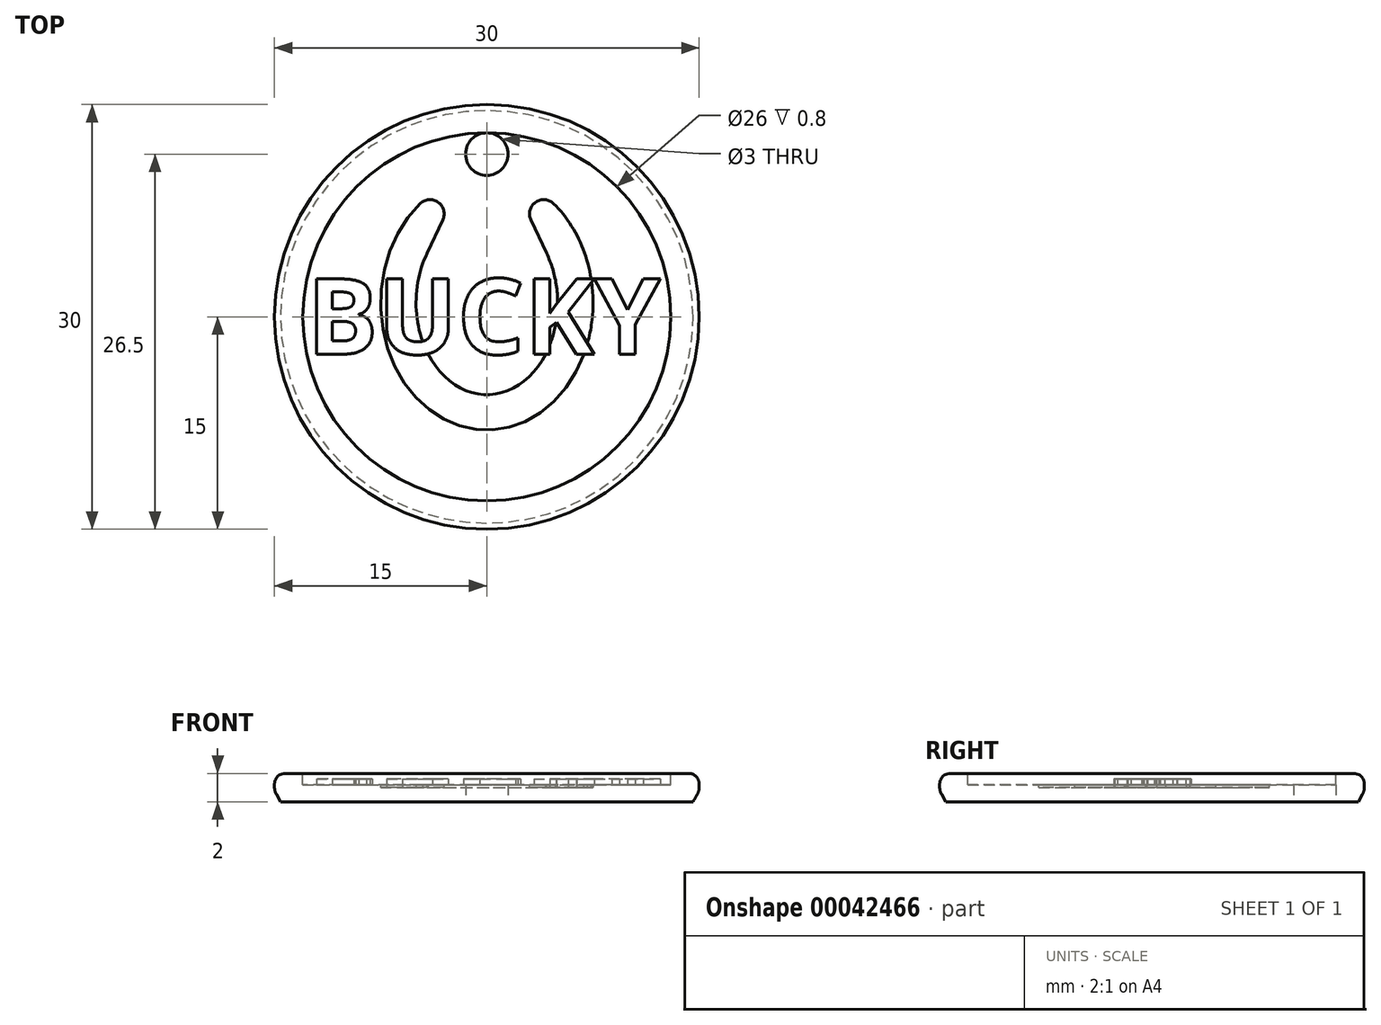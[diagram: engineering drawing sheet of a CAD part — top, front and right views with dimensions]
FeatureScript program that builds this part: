
annotation { "Feature Type Name" : "Feature", "Feature Type Description" : "" }
export const myFeature = defineFeature(function(context is Context, id is Id, definition is map)
    precondition{}
    {
        {
            var Q0;
            Q0=qCreatedBy(makeId("Top.planeOp"),FACE);
            var sketch = newSketch(context, id + "F0", { "sketchPlane" : qUnion([Q0])});
            skCircle(sketch, "E0", {"center": v(0, 0) * mm, "radius": 15 * mm});
            skSolve(sketch);
        }
        {
            var Q0;
            Q0=qSketchRegion(id+"F0",true);
            extrude(context, id + "F1", {"entities" : qUnion([Q0]), "depth" : 2 * mm});
        }
        {
            var Q0;
            Q0=makeQuery(id+"F1.opExtrude","CAP_FACE",FACE,{"disambiguationData":[OSD([sQuery(id+"F0.wireOp",EDGE,"E0")])],"isStart":false});
            var sketch = newSketch(context, id + "F2", { "sketchPlane" : qUnion([Q0])});
            skCircle(sketch, "E1", {"center": v(0, 0) * mm, "radius": 13 * mm});
            skSolve(sketch);
        }
        {
            var Q0;
            Q0=qSketchRegion(id+"F2",true);
            extrude(context, id + "F3", {"entities" : qUnion([Q0]), "operationType" : NewBodyOperationType.REMOVE, "oppositeDirection" : true, "depth" : 0.8 * mm});
        }
        {
            var Q0;
            Q0=makeQuery(id+"F3.boolean.opBoolean","COPY",FACE,{"derivedFrom":makeQuery(id+"F3.opExtrude","CAP_FACE",FACE,{"disambiguationData":[OSD([sQuery(id+"F2.wireOp",EDGE,"E1")])],"isStart":false})});
            var sketch = newSketch(context, id + "F4", { "sketchPlane" : qUnion([Q0])});
            skLineSegment(sketch, "E2", {"start": v(-7.5, -8) * mm, "end": v(7.5, 8) * mm, "construction": true});
            skEllipticalArc(sketch, "E3", {});
            skEllipticalArc(sketch, "E4", {});
            skLineSegment(sketch, "E5", {"start": v(-4.21, 4.5) * mm, "end": v(-3.11, 6.86) * mm});
            skArc(sketch, "E6", {"start": v(-3.11, 6.86) * mm, "mid": v(-3.44, 8.1) * mm, "end": v(-4.72, 8) * mm});
            skArc(sketch, "E7.MirrorCS", {"start": v(3.11, 6.86) * mm, "mid": v(3.44, 8.1) * mm, "end": v(4.72, 8) * mm});
            skLineSegment(sketch, "E8.MirrorCS", {"start": v(4.21, 4.5) * mm, "end": v(3.11, 6.86) * mm});
            const initialGuessF4  = {"E3": [0, 0.001, 0, -1, 0.0065, 0.005, 4.143778680120507, 2.1394066270590786], "E4": [0, 0.001, 0, -1, 0.009, 0.0075, 3.821776784577257, 2.461408522602329]};
            skSetInitialGuess(sketch, initialGuessF4);
            skSolve(sketch);
        }
        {
            var Q0;
            Q0=qSketchRegion(id+"F4",true);
            extrude(context, id + "F5", {"entities" : qUnion([Q0]), "operationType" : NewBodyOperationType.REMOVE, "oppositeDirection" : true, "depth" : 0.2 * mm});
        }
        {
            var Q0;
            Q0=qCreatedBy(makeId("Top.planeOp"),FACE);
            var sketch = newSketch(context, id + "F6", { "sketchPlane" : qUnion([Q0])});
            skLineSegment(sketch, "E9", {"start": v(0, 0.05) * mm, "end": v(0, -0.05) * mm, "construction": true});
            skSolve(sketch);
        }
        {
            var Q0;
            Q0=makeQuery(id+"F3.boolean.opBoolean","COPY",FACE,{"derivedFrom":makeQuery(id+"F3.opExtrude","CAP_FACE",FACE,{"disambiguationData":[OSD([sQuery(id+"F2.wireOp",EDGE,"E1")])],"isStart":false})});
            var sketch = newSketch(context, id + "F7", { "sketchPlane" : qUnion([Q0])});
            skText(sketch, "E10", { "text": "BUCKY", "fontName": "OpenSans-Bold.ttf"});
            const initialGuessF7  = {"E10": [-0.01271, -0.00263, 1, 0, 0.00536]};
            skSetInitialGuess(sketch, initialGuessF7);
            skSolve(sketch);
        }
        {
            var Q0;
            Q0=qSketchRegion(id+"F7",true);
            extrude(context, id + "F8", {"entities" : qUnion([Q0]), "operationType" : NewBodyOperationType.ADD, "depth" : 0.4 * mm, "hasSecondDirection" : true, "secondDirectionOppositeDirection" : true, "secondDirectionDepth" : 0.5 * mm});
        }
        {
            var Q0;
            Q0=qCreatedBy(makeId("Top.planeOp"),FACE);
            var sketch = newSketch(context, id + "F9", { "sketchPlane" : qUnion([Q0])});
            skCircle(sketch, "E11", {"center": v(0, 11.5) * mm, "radius": 1.5 * mm});
            skSolve(sketch);
        }
        {
            var Q0;
            Q0=qSketchRegion(id+"F9",true);
            extrude(context, id + "F10", {"entities" : qUnion([Q0]), "operationType" : NewBodyOperationType.REMOVE, "endBound" : BoundingType.THROUGH_ALL, "depth" : 25 * mm});
        }
        {
            var Q0;
            Q0=makeQuery(id+"F8.opExtrude","CAP_EDGE",EDGE,{"disambiguationData":[OSD([sQuery(id+"F0.wireOp",EDGE,"E0")])],"isStart":false});
            var Q1;
            Q1=makeQuery(id+"F8.opExtrude","CAP_EDGE",EDGE,{"disambiguationData":[OSD([sQuery(id+"F2.wireOp",EDGE,"E1")])],"isStart":false});
            var Q2;
            Q2=makeQuery(id+"F1.opExtrude","CAP_EDGE",EDGE,{"disambiguationData":[OSD([sQuery(id+"F0.wireOp",EDGE,"E0")])],"isStart":false});
            var Q3;
            Q3=makeQuery(id+"F3.boolean.opBoolean","COPY",EDGE,{"derivedFrom":makeQuery(id+"F3.opExtrude","CAP_EDGE",EDGE,{"disambiguationData":[OSD([sQuery(id+"F2.wireOp",EDGE,"E1")])],"isStart":true})});
            fillet(context, id + "F11", {"entities" : qUnion([Q0, Q1, Q2, Q3]), "radius" : 0.75 * mm, "tangentPropagation" : true, "allowEdgeOverflow" : false});
        }
        {
            var Q0;
            Q0=makeQuery(id+"F1.opExtrude","CAP_EDGE",EDGE,{"disambiguationData":[OSD([sQuery(id+"F0.wireOp",EDGE,"E0")])],"isStart":true});
            chamfer(context, id + "F12", {"entities" : qUnion([Q0]), "chamferType" : ChamferType.OFFSET_ANGLE, "width" : 0.75 * mm, "oppositeDirection" : false, "angle" : 30 * degree, "tangentPropagation" : true});
        }
        {
            var Q0;
            {var subQ0=sQuery(id+"F0.wireOp",EDGE,"E0");Q0=makeQuery(id+"F12.opChamfer","BLEND_EDGE",EDGE,{"blendedFrom":[makeQuery(id+"F1.opExtrude","CAP_EDGE",EDGE,{"disambiguationData":[OSD([subQ0])],"isStart":true}),makeQuery(id+"F8.boolean.opBoolean","MERGE",FACE,{"derivedFrom":[makeQuery(id+"F1.opExtrude","SWEPT_FACE",FACE,{"disambiguationData":[OSD([subQ0])]}),makeQuery(id+"F8.opExtrude","SWEPT_FACE",FACE,{"disambiguationData":[OSD([subQ0])]})]})],"blendedInto":[makeQuery(id+"F8.boolean.opBoolean","MERGE",FACE,{"derivedFrom":[makeQuery(id+"F1.opExtrude","SWEPT_FACE",FACE,{"disambiguationData":[OSD([subQ0])]}),makeQuery(id+"F8.opExtrude","SWEPT_FACE",FACE,{"disambiguationData":[OSD([subQ0])]})]})]});}
            fillet(context, id + "F13", {"entities" : qUnion([Q0]), "radius" : 1 * mm, "tangentPropagation" : true, "allowEdgeOverflow" : false});
        }
    });
